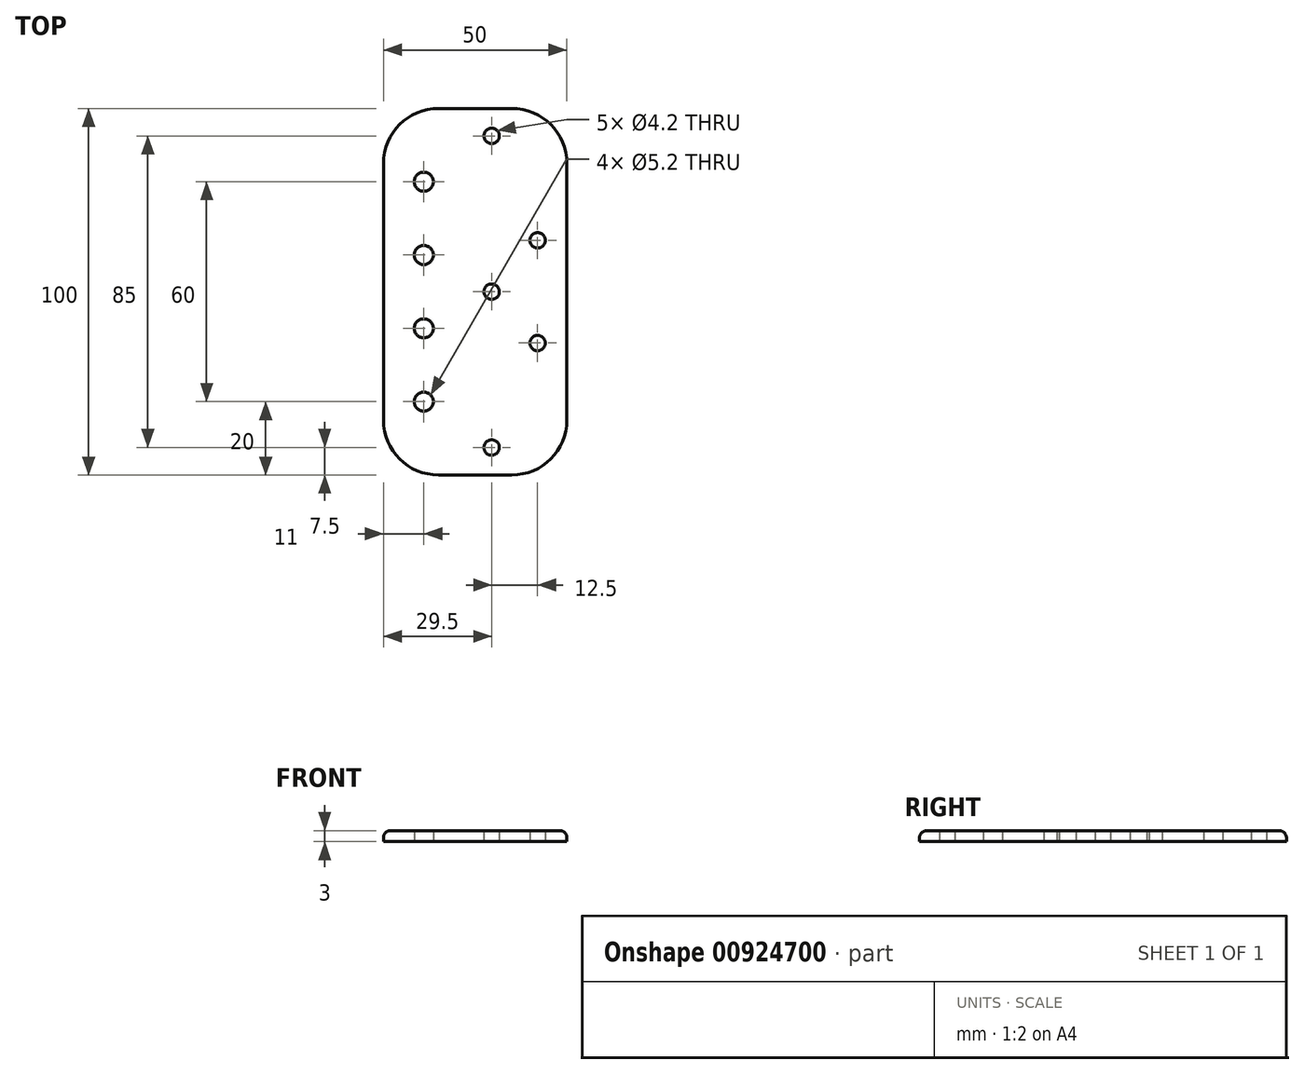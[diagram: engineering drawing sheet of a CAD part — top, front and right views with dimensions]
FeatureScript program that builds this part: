
annotation { "Feature Type Name" : "Feature", "Feature Type Description" : "" }
export const myFeature = defineFeature(function(context is Context, id is Id, definition is map)
    precondition{}
    {
        {
            var Q0;
            Q0=qCreatedBy(makeId("Top.planeOp"),FACE);
            var sketch = newSketch(context, id + "F0", { "sketchPlane" : qUnion([Q0])});
            skLineSegment(sketch, "E0.bottom", {"start": v(-29.5, 50) * mm, "end": v(20.5, 50) * mm});
            skLineSegment(sketch, "E0.top", {"start": v(-29.5, -50) * mm, "end": v(20.5, -50) * mm});
            skLineSegment(sketch, "E0.left", {"start": v(-29.5, 50) * mm, "end": v(-29.5, -50) * mm});
            skLineSegment(sketch, "E0.right", {"start": v(20.5, 50) * mm, "end": v(20.5, -50) * mm});
            skCircle(sketch, "E1", {"center": v(0, 42.5) * mm, "radius": 2.1 * mm});
            skCircle(sketch, "E2", {"center": v(0, 0) * mm, "radius": 2.1 * mm});
            skCircle(sketch, "E3", {"center": v(0, -42.5) * mm, "radius": 2.1 * mm});
            skCircle(sketch, "E4", {"center": v(12.5, 14) * mm, "radius": 2.1 * mm});
            skCircle(sketch, "E5", {"center": v(12.5, -14) * mm, "radius": 2.1 * mm});
            skLineSegment(sketch, "E6", {"start": v(0, -42.5) * mm, "end": v(0, 42.5) * mm, "construction": true});
            skLineSegment(sketch, "E7", {"start": v(0, -42.5) * mm, "end": v(0, -50) * mm, "construction": true});
            skLineSegment(sketch, "E8", {"start": v(0, 42.5) * mm, "end": v(0, 50) * mm, "construction": true});
            skLineSegment(sketch, "E9", {"start": v(-7.5, 50) * mm, "end": v(-7.5, -50) * mm, "construction": true});
            skCircle(sketch, "E10", {"center": v(-18.5, 30) * mm, "radius": 2.6 * mm});
            skCircle(sketch, "E11", {"center": v(-18.5, 10) * mm, "radius": 2.6 * mm});
            skCircle(sketch, "E12", {"center": v(-18.5, -10) * mm, "radius": 2.6 * mm});
            skCircle(sketch, "E13", {"center": v(-18.5, -30) * mm, "radius": 2.6 * mm});
            skLineSegment(sketch, "E14", {"start": v(-18.5, -30) * mm, "end": v(-18.5, -50) * mm, "construction": true});
            skLineSegment(sketch, "E15", {"start": v(-18.5, 30) * mm, "end": v(-18.5, 50) * mm, "construction": true});
            skSolve(sketch);
        }
        {
            var Q0;
            Q0=makeQuery(id+"F0.imprint","IMPRINT",FACE,{"disambiguationData":[TD([[makeQuery(id+"F0.imprint","IMPRINT",EDGE,{"derivedFrom":sQuery(id+"F0.wireOp",EDGE,"E0.bottom")}),-1.0]])]});
            extrude(context, id + "F1", {"entities" : qUnion([Q0]), "depth" : 3 * mm, "offsetDistance" : 25 * mm});
        }
        {
            var Q0;
            Q0=makeQuery(id+"F1.opExtrude","SWEPT_EDGE",EDGE,{"disambiguationData":[OSD([sQuery(id+"F0.wireOp",EDGE,"E0.top"),sQuery(id+"F0.wireOp",EDGE,"E0.left")])]});
            var Q1;
            Q1=makeQuery(id+"F1.opExtrude","SWEPT_EDGE",EDGE,{"disambiguationData":[OSD([sQuery(id+"F0.wireOp",EDGE,"E0.top"),sQuery(id+"F0.wireOp",EDGE,"E0.right")])]});
            var Q2;
            Q2=makeQuery(id+"F1.opExtrude","SWEPT_EDGE",EDGE,{"disambiguationData":[OSD([sQuery(id+"F0.wireOp",EDGE,"E0.bottom"),sQuery(id+"F0.wireOp",EDGE,"E0.right")])]});
            var Q3;
            Q3=makeQuery(id+"F1.opExtrude","SWEPT_EDGE",EDGE,{"disambiguationData":[OSD([sQuery(id+"F0.wireOp",EDGE,"E0.bottom"),sQuery(id+"F0.wireOp",EDGE,"E0.left")])]});
            fillet(context, id + "F2", {"entities" : qUnion([Q0, Q1, Q2, Q3]), "radius" : 15 * mm, "tangentPropagation" : true, "allowEdgeOverflow" : false});
        }
        {
            var Q0;
            Q0=makeQuery(id+"F1.opExtrude","CAP_EDGE",EDGE,{"disambiguationData":[OSD([sQuery(id+"F0.wireOp",EDGE,"E0.bottom")])],"isStart":false});
            fillet(context, id + "F3", {"entities" : qUnion([Q0]), "radius" : 2 * mm, "tangentPropagation" : true, "allowEdgeOverflow" : false});
        }
    });
